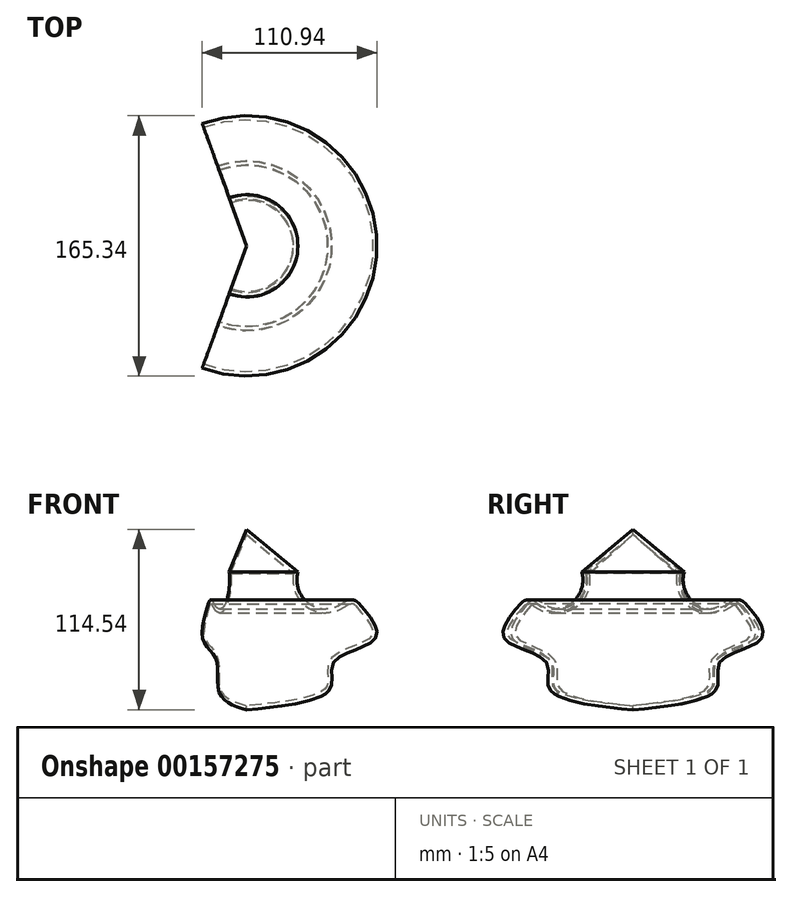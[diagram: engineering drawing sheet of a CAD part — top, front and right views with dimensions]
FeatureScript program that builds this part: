
annotation { "Feature Type Name" : "Feature", "Feature Type Description" : "" }
export const myFeature = defineFeature(function(context is Context, id is Id, definition is map)
    precondition{}
    {
        {
            var Q0;
            Q0=qCreatedBy(makeId("Front.planeOp"),FACE);
            var sketch = newSketch(context, id + "F0", { "sketchPlane" : qUnion([Q0])});
            skLineSegment(sketch, "E0", {"start": v(0, 0) * mm, "end": v(0, 114.54) * mm});
            skLineSegment(sketch, "E1", {"start": v(0, 114.54) * mm, "end": v(32.51, 87.49) * mm});
            skArc(sketch, "E2", {"start": v(32.51, 87.49) * mm, "mid": v(40.28, 67.02) * mm, "end": v(62.13, 68.45) * mm});
            skFitSpline(sketch, "E3", {"points": [v(66.1, 73.14) * mm, v(81.66, 45.36) * mm, v(55.4, 30.7) * mm, v(53.27, 13.92) * mm, v(0, 0) * mm], "startDerivative": vector(119.36, -128.82) * mm, "endDerivative": vector(-224.04, -22.3) * mm});
            skArc(sketch, "E4.filletArc", {"start": v(70.95, 67.85) * mm, "mid": v(66.66, 69.94) * mm, "end": v(62.13, 68.45) * mm});
            skSolve(sketch);
        }
        {
            var Q0;
            Q0 = qSketchRegion(id + "F0", true);
            var Q1;
            Q1=sQuery(id+"F0.wireOp",EDGE,"E0");
            revolve(context, id + "F1", {"surfaceOperationType" : NewSurfaceOperationType.NEW, "entities" : qUnion([Q0]), "axis" : qUnion([Q1]), "revolveType" : RevolveType.SYMMETRIC, "angle" : 220 * degree});
        }
        {
            var Q0;
            Q0=makeQuery(id+"F1.opRevolve","CAP_FACE",FACE,{"disambiguationData":[OSD([sQuery(id+"F0.wireOp",EDGE,"E0"),sQuery(id+"F0.wireOp",EDGE,"E1"),sQuery(id+"F0.wireOp",EDGE,"E2"),sQuery(id+"F0.wireOp",EDGE,"E3"),sQuery(id+"F0.wireOp",EDGE,"E4.filletArc")])],"isStart":true});
            var Q1;
            Q1=makeQuery(id+"F1.opRevolve","CAP_FACE",FACE,{"disambiguationData":[OSD([sQuery(id+"F0.wireOp",EDGE,"E0"),sQuery(id+"F0.wireOp",EDGE,"E1"),sQuery(id+"F0.wireOp",EDGE,"E2"),sQuery(id+"F0.wireOp",EDGE,"E3"),sQuery(id+"F0.wireOp",EDGE,"E4.filletArc")])],"isStart":false});
            shell(context, id + "F2", {"entities" : qUnion([Q0, Q1]), "thickness" : 2.54 * mm});
        }
    });
